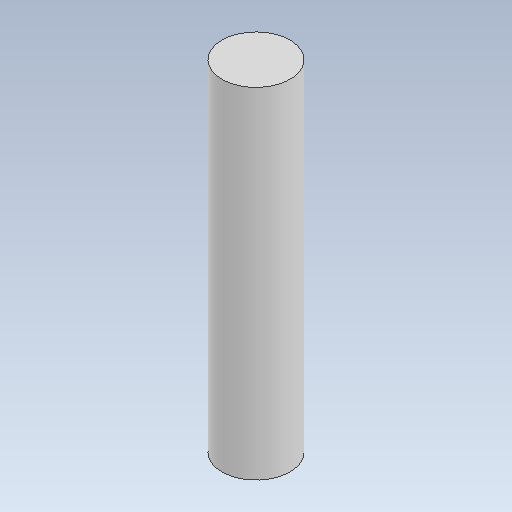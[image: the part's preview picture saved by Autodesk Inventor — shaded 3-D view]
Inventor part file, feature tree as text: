
AUTODESK INVENTOR PART (.ipt)
format: ipt  version: 2020 (Build 240168000, 168)  size: 73,728 bytes
history: native  units: mm
features: other x3, sketch x1
ambient origin geometry x8: Origin, YZ Plane, XZ Plane, XY Plane, X Axis, Y Axis, Z Axis, Center Point
bodies: Solid1 (feature_tree)
feature tree (4):
  other  "pin_3_15.ipt"
  other  "Solid1::pin_3_15.ipt"
  other  "TaggingFeature1"
  sketch  "Sketch1"  dims[d0=10.0mm]
